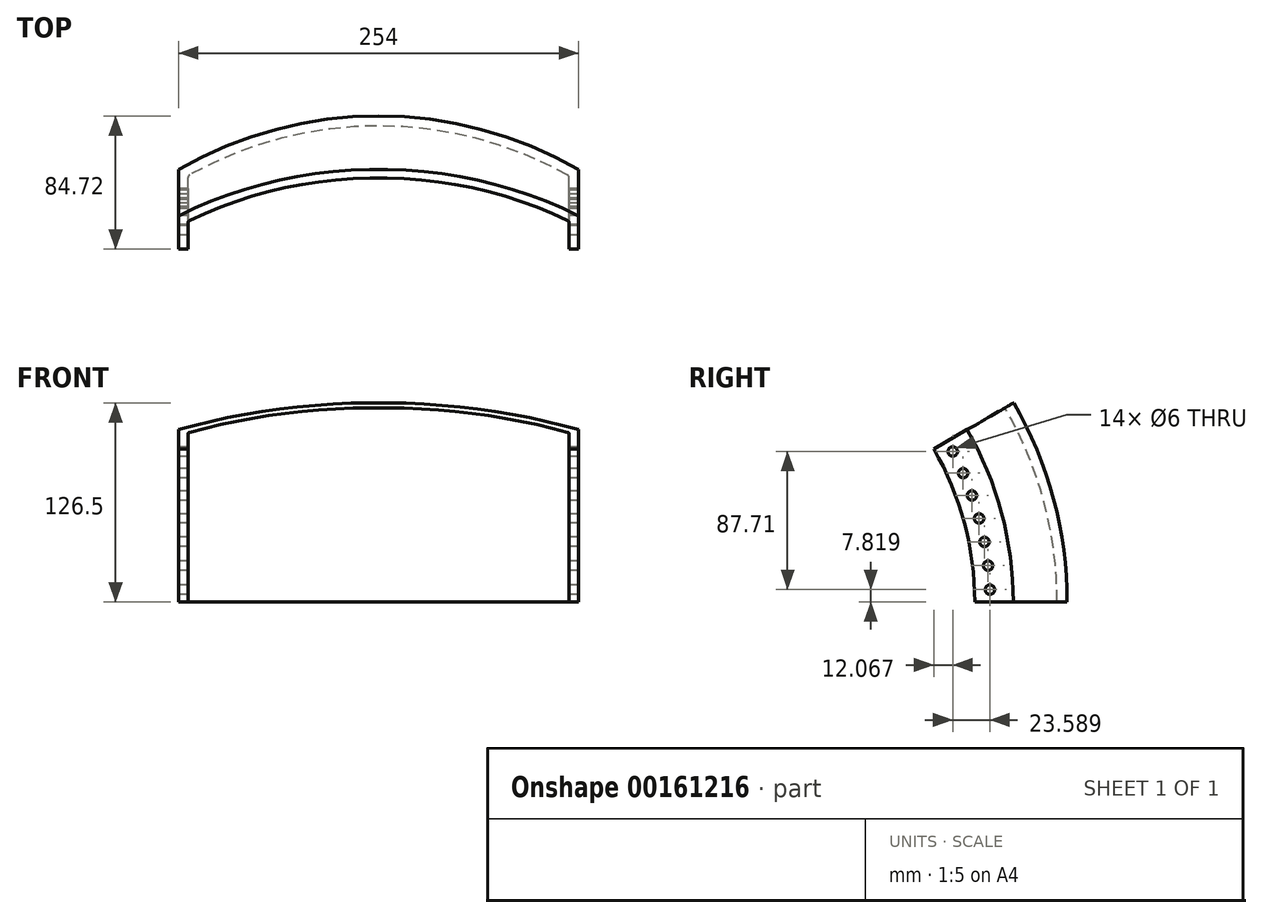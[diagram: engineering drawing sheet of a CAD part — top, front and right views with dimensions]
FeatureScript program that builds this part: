
annotation { "Feature Type Name" : "Feature", "Feature Type Description" : "" }
export const myFeature = defineFeature(function(context is Context, id is Id, definition is map)
    precondition{}
    {
        {
            var Q0;
            Q0=qCreatedBy(makeId("Top.planeOp"),FACE);
            var sketch = newSketch(context, id + "F0", { "sketchPlane" : qUnion([Q0])});
            skArc(sketch, "E0", {"start": v(127, 218.81) * mm, "mid": v(0, 253) * mm, "end": v(-127, 218.81) * mm});
            skLineSegment(sketch, "E1", {"start": v(0, 253) * mm, "end": v(127, 253) * mm, "construction": true});
            skLineSegment(sketch, "E2", {"start": v(127, 253) * mm, "end": v(127, 218.81) * mm, "construction": true});
            skLineSegment(sketch, "E3", {"start": v(127, 218.81) * mm, "end": v(127, 194.31) * mm});
            skLineSegment(sketch, "E4", {"start": v(127, 194.31) * mm, "end": v(121, 194.31) * mm});
            skLineSegment(sketch, "E5", {"start": v(121, 194.31) * mm, "end": v(121, 214.93) * mm});
            skLineSegment(sketch, "E6.MirrorCS", {"start": v(-121, 194.31) * mm, "end": v(-121, 214.93) * mm});
            skLineSegment(sketch, "E7.MirrorCS", {"start": v(-127, 218.81) * mm, "end": v(-127, 194.31) * mm});
            skLineSegment(sketch, "E8.MirrorCS", {"start": v(-127, 194.31) * mm, "end": v(-121, 194.31) * mm});
            skPoint(sketch, "E9.MirrorCS.end.orphan", {"position": v(-127, 218.81) * mm});
            skPoint(sketch, "E9.MirrorCS.start.orphan", {"position": v(-127, 253) * mm});
            skPoint(sketch, "E10.MirrorCS.start.orphan", {"position": v(0, 253) * mm});
            skLineSegment(sketch, "E11", {"start": v(0, 0) * mm, "end": v(139.33, 0) * mm, "construction": true});
            skLineSegment(sketch, "E12", {"start": v(0, 253) * mm, "end": v(0, 246.65) * mm});
            skPoint(sketch, "E13.orphan", {"position": v(121, 210.73) * mm});
            skPoint(sketch, "E14.orphan", {"position": v(-121, 210.73) * mm});
            skArc(sketch, "E15.trimOffspring", {"start": v(121, 214.93) * mm, "mid": v(0, 246.65) * mm, "end": v(-121, 214.93) * mm});
            skSolve(sketch);
        }
        {
            var Q0;
            Q0=qSketchRegion(id+"F0",true);
            var Q1;
            Q1=sQuery(id+"F0.wireOp",EDGE,"E11");
            revolve(context, id + "F1", {"entities" : qUnion([Q0]), "axis" : qUnion([Q1]), "revolveType" : RevolveType.ONE_DIRECTION, "angle" : 30 * degree});
        }
        {
            var Q0;
            Q0=makeQuery(id+"F1.opRevolve","SWEPT_EDGE",EDGE,{"disambiguationData":[OSD([sQuery(id+"F0.wireOp",EDGE,"E5"),sQuery(id+"F0.wireOp",EDGE,"E15.trimOffspring")])]});
            fillet(context, id + "F2", {"entities" : qUnion([Q0]), "radius" : 2 * mm, "tangentPropagation" : true, "allowEdgeOverflow" : false});
        }
        {
            var Q0;
            Q0=makeQuery(id+"F1.opRevolve","SWEPT_EDGE",EDGE,{"disambiguationData":[OSD([sQuery(id+"F0.wireOp",EDGE,"E6.MirrorCS"),sQuery(id+"F0.wireOp",EDGE,"E15.trimOffspring")])]});
            fillet(context, id + "F3", {"entities" : qUnion([Q0]), "radius" : 2 * mm, "tangentPropagation" : true, "allowEdgeOverflow" : false});
        }
        {
            var Q0;
            Q0=makeQuery(id+"F1.opRevolve","SWEPT_FACE",FACE,{"disambiguationData":[OSD([sQuery(id+"F0.wireOp",EDGE,"E7.MirrorCS")])]});
            var sketch = newSketch(context, id + "F4", { "sketchPlane" : qUnion([Q0])});
            skLineSegment(sketch, "E16", {"start": v(-218.81, 0) * mm, "end": v(0, 0) * mm});
            skLineSegment(sketch, "E17", {"start": v(-194.31, 0) * mm, "end": v(-194.17, 7.63) * mm});
            skLineSegment(sketch, "E18", {"start": v(-218.81, 0) * mm, "end": v(-194.31, 0) * mm});
            skLineSegment(sketch, "E19.1.0", {"start": v(-218.67, 8.35) * mm, "end": v(-194.19, 7.44) * mm});
            skPoint(sketch, "E19.center", {"position": v(4.56, 0.27) * mm});
            skLineSegment(sketch, "E19.anchor1", {"start": v(4.56, 0.27) * mm, "end": v(-218.81, 0) * mm, "construction": true});
            skLineSegment(sketch, "E19.anchor2", {"start": v(4.56, 0.27) * mm, "end": v(-218.67, 8.35) * mm, "construction": true});
            skLineSegment(sketch, "E20", {"start": v(-194.17, 7.63) * mm, "end": v(-203.94, 7.82) * mm});
            skCircle(sketch, "E21", {"center": v(-203.94, 7.82) * mm, "radius": 3 * mm});
            skCircle(sketch, "E22.1.0", {"center": v(-203.95, -7.44) * mm, "radius": 3 * mm});
            skCircle(sketch, "E22.2.0", {"center": v(-202.82, -22.66) * mm, "radius": 3 * mm});
            skCircle(sketch, "E22.3.0", {"center": v(-200.56, -37.76) * mm, "radius": 3 * mm});
            skCircle(sketch, "E22.4.0", {"center": v(-197.18, -52.64) * mm, "radius": 3 * mm});
            skCircle(sketch, "E22.5.0", {"center": v(-192.7, -67.23) * mm, "radius": 3 * mm});
            skCircle(sketch, "E22.6.0", {"center": v(-187.13, -81.44) * mm, "radius": 3 * mm});
            skCircle(sketch, "E22.7.0", {"center": v(-180.52, -95.2) * mm, "radius": 3 * mm});
            skCircle(sketch, "E22.8.0", {"center": v(-172.9, -108.42) * mm, "radius": 3 * mm});
            skCircle(sketch, "E22.9.0", {"center": v(-164.32, -121.04) * mm, "radius": 3 * mm});
            skCircle(sketch, "E22.10.0", {"center": v(-154.81, -132.98) * mm, "radius": 3 * mm});
            skCircle(sketch, "E22.11.0", {"center": v(-144.44, -144.18) * mm, "radius": 3 * mm});
            skCircle(sketch, "E22.12.0", {"center": v(-133.27, -154.57) * mm, "radius": 3 * mm});
            skCircle(sketch, "E22.13.0", {"center": v(-121.34, -164.1) * mm, "radius": 3 * mm});
            skCircle(sketch, "E22.14.0", {"center": v(-108.74, -172.7) * mm, "radius": 3 * mm});
            skCircle(sketch, "E22.15.0", {"center": v(-95.53, -180.35) * mm, "radius": 3 * mm});
            skCircle(sketch, "E22.16.0", {"center": v(-81.78, -186.98) * mm, "radius": 3 * mm});
            skCircle(sketch, "E22.17.0", {"center": v(-67.58, -192.57) * mm, "radius": 3 * mm});
            skCircle(sketch, "E22.18.0", {"center": v(-53, -197.08) * mm, "radius": 3 * mm});
            skCircle(sketch, "E22.19.0", {"center": v(-38.13, -200.5) * mm, "radius": 3 * mm});
            skCircle(sketch, "E22.20.0", {"center": v(-23.04, -202.78) * mm, "radius": 3 * mm});
            skCircle(sketch, "E22.21.0", {"center": v(-7.82, -203.94) * mm, "radius": 3 * mm});
            skCircle(sketch, "E22.22.0", {"center": v(7.44, -203.95) * mm, "radius": 3 * mm});
            skCircle(sketch, "E22.23.0", {"center": v(22.66, -202.82) * mm, "radius": 3 * mm});
            skCircle(sketch, "E22.24.0", {"center": v(37.76, -200.56) * mm, "radius": 3 * mm});
            skCircle(sketch, "E22.25.0", {"center": v(52.64, -197.18) * mm, "radius": 3 * mm});
            skCircle(sketch, "E22.26.0", {"center": v(67.23, -192.7) * mm, "radius": 3 * mm});
            skCircle(sketch, "E22.27.0", {"center": v(81.44, -187.13) * mm, "radius": 3 * mm});
            skCircle(sketch, "E22.28.0", {"center": v(95.2, -180.52) * mm, "radius": 3 * mm});
            skCircle(sketch, "E22.29.0", {"center": v(108.42, -172.9) * mm, "radius": 3 * mm});
            skCircle(sketch, "E22.30.0", {"center": v(121.04, -164.32) * mm, "radius": 3 * mm});
            skCircle(sketch, "E22.31.0", {"center": v(132.98, -154.81) * mm, "radius": 3 * mm});
            skCircle(sketch, "E22.32.0", {"center": v(144.18, -144.44) * mm, "radius": 3 * mm});
            skCircle(sketch, "E22.33.0", {"center": v(154.57, -133.27) * mm, "radius": 3 * mm});
            skCircle(sketch, "E22.34.0", {"center": v(164.1, -121.34) * mm, "radius": 3 * mm});
            skCircle(sketch, "E22.35.0", {"center": v(172.7, -108.74) * mm, "radius": 3 * mm});
            skCircle(sketch, "E22.36.0", {"center": v(180.35, -95.53) * mm, "radius": 3 * mm});
            skCircle(sketch, "E22.37.0", {"center": v(186.98, -81.78) * mm, "radius": 3 * mm});
            skCircle(sketch, "E22.38.0", {"center": v(192.57, -67.58) * mm, "radius": 3 * mm});
            skCircle(sketch, "E22.39.0", {"center": v(197.08, -53) * mm, "radius": 3 * mm});
            skCircle(sketch, "E22.40.0", {"center": v(200.5, -38.13) * mm, "radius": 3 * mm});
            skCircle(sketch, "E22.41.0", {"center": v(202.78, -23.04) * mm, "radius": 3 * mm});
            skCircle(sketch, "E22.42.0", {"center": v(203.94, -7.82) * mm, "radius": 3 * mm});
            skCircle(sketch, "E22.43.0", {"center": v(203.95, 7.44) * mm, "radius": 3 * mm});
            skCircle(sketch, "E22.44.0", {"center": v(202.82, 22.66) * mm, "radius": 3 * mm});
            skCircle(sketch, "E22.45.0", {"center": v(200.56, 37.76) * mm, "radius": 3 * mm});
            skCircle(sketch, "E22.46.0", {"center": v(197.18, 52.64) * mm, "radius": 3 * mm});
            skCircle(sketch, "E22.47.0", {"center": v(192.7, 67.23) * mm, "radius": 3 * mm});
            skCircle(sketch, "E22.48.0", {"center": v(187.13, 81.44) * mm, "radius": 3 * mm});
            skCircle(sketch, "E22.49.0", {"center": v(180.52, 95.2) * mm, "radius": 3 * mm});
            skCircle(sketch, "E22.50.0", {"center": v(172.9, 108.42) * mm, "radius": 3 * mm});
            skCircle(sketch, "E22.51.0", {"center": v(164.32, 121.04) * mm, "radius": 3 * mm});
            skCircle(sketch, "E22.52.0", {"center": v(154.81, 132.98) * mm, "radius": 3 * mm});
            skCircle(sketch, "E22.53.0", {"center": v(144.44, 144.18) * mm, "radius": 3 * mm});
            skCircle(sketch, "E22.54.0", {"center": v(133.27, 154.57) * mm, "radius": 3 * mm});
            skCircle(sketch, "E22.55.0", {"center": v(121.34, 164.1) * mm, "radius": 3 * mm});
            skCircle(sketch, "E22.56.0", {"center": v(108.74, 172.7) * mm, "radius": 3 * mm});
            skCircle(sketch, "E22.57.0", {"center": v(95.53, 180.35) * mm, "radius": 3 * mm});
            skCircle(sketch, "E22.58.0", {"center": v(81.78, 186.98) * mm, "radius": 3 * mm});
            skCircle(sketch, "E22.59.0", {"center": v(67.58, 192.57) * mm, "radius": 3 * mm});
            skCircle(sketch, "E22.60.0", {"center": v(53, 197.08) * mm, "radius": 3 * mm});
            skCircle(sketch, "E22.61.0", {"center": v(38.13, 200.5) * mm, "radius": 3 * mm});
            skCircle(sketch, "E22.62.0", {"center": v(23.04, 202.78) * mm, "radius": 3 * mm});
            skCircle(sketch, "E22.63.0", {"center": v(7.82, 203.94) * mm, "radius": 3 * mm});
            skCircle(sketch, "E22.64.0", {"center": v(-7.44, 203.95) * mm, "radius": 3 * mm});
            skCircle(sketch, "E22.65.0", {"center": v(-22.66, 202.82) * mm, "radius": 3 * mm});
            skCircle(sketch, "E22.66.0", {"center": v(-37.76, 200.56) * mm, "radius": 3 * mm});
            skCircle(sketch, "E22.67.0", {"center": v(-52.64, 197.18) * mm, "radius": 3 * mm});
            skCircle(sketch, "E22.68.0", {"center": v(-67.23, 192.7) * mm, "radius": 3 * mm});
            skCircle(sketch, "E22.69.0", {"center": v(-81.44, 187.13) * mm, "radius": 3 * mm});
            skCircle(sketch, "E22.70.0", {"center": v(-95.2, 180.52) * mm, "radius": 3 * mm});
            skCircle(sketch, "E22.71.0", {"center": v(-108.42, 172.9) * mm, "radius": 3 * mm});
            skCircle(sketch, "E22.72.0", {"center": v(-121.04, 164.32) * mm, "radius": 3 * mm});
            skCircle(sketch, "E22.73.0", {"center": v(-132.98, 154.81) * mm, "radius": 3 * mm});
            skCircle(sketch, "E22.74.0", {"center": v(-144.18, 144.44) * mm, "radius": 3 * mm});
            skCircle(sketch, "E22.75.0", {"center": v(-154.57, 133.27) * mm, "radius": 3 * mm});
            skCircle(sketch, "E22.76.0", {"center": v(-164.1, 121.34) * mm, "radius": 3 * mm});
            skCircle(sketch, "E22.77.0", {"center": v(-172.7, 108.74) * mm, "radius": 3 * mm});
            skCircle(sketch, "E22.78.0", {"center": v(-180.35, 95.53) * mm, "radius": 3 * mm});
            skCircle(sketch, "E22.79.0", {"center": v(-186.98, 81.78) * mm, "radius": 3 * mm});
            skCircle(sketch, "E22.80.0", {"center": v(-192.57, 67.58) * mm, "radius": 3 * mm});
            skCircle(sketch, "E22.81.0", {"center": v(-197.08, 53) * mm, "radius": 3 * mm});
            skCircle(sketch, "E22.82.0", {"center": v(-200.5, 38.13) * mm, "radius": 3 * mm});
            skCircle(sketch, "E22.83.0", {"center": v(-202.78, 23.04) * mm, "radius": 3 * mm});
            skPoint(sketch, "E22.center", {"position": v(0, 0) * mm});
            skLineSegment(sketch, "E23", {"start": v(0, 0) * mm, "end": v(-200.5, 38.13) * mm});
            skLineSegment(sketch, "E24", {"start": v(0, 0) * mm, "end": v(-202.78, 23.04) * mm});
            skSolve(sketch);
        }
        {
            var Q0;
            Q0 = qSketchRegion(id + "F4", true);
            extrude(context, id + "F5", {"entities" : qUnion([Q0]), "operationType" : NewBodyOperationType.REMOVE, "endBound" : BoundingType.THROUGH_ALL, "oppositeDirection" : true, "depth" : 25 * mm});
        }
    });
